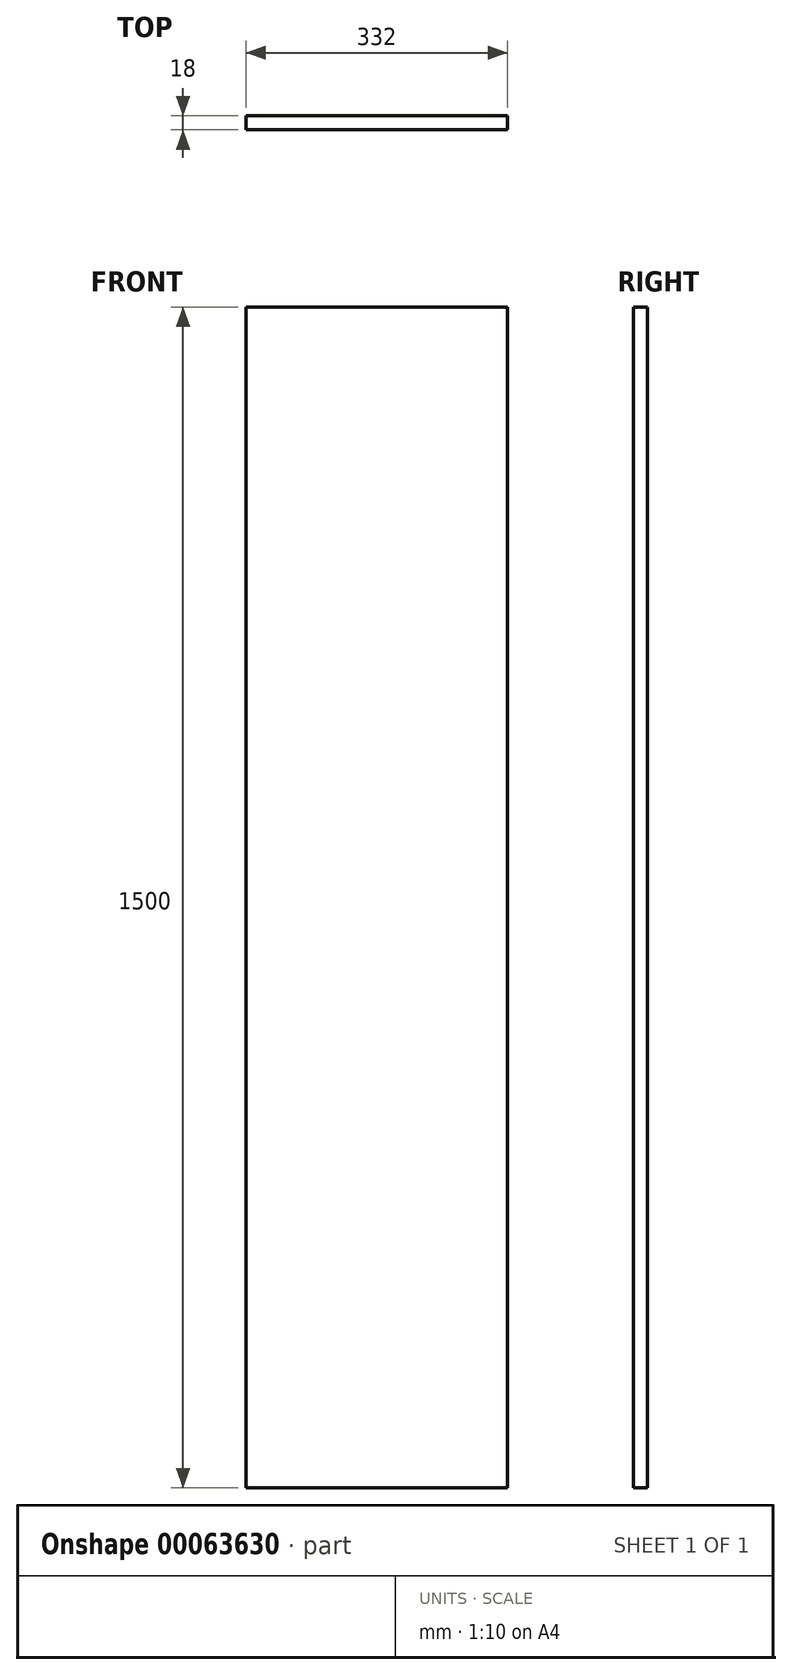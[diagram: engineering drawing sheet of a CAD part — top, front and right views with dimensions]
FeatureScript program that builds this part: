
annotation { "Feature Type Name" : "Feature", "Feature Type Description" : "" }
export const myFeature = defineFeature(function(context is Context, id is Id, definition is map)
    precondition{}
    {
        {
            var Q0;
            Q0=qCreatedBy(makeId("Front.planeOp"),FACE);
            var sketch = newSketch(context, id + "F0", { "sketchPlane" : qUnion([Q0])});
            skLineSegment(sketch, "E0.bottom", {"start": v(0, 0) * mm, "end": v(332, 0) * mm});
            skLineSegment(sketch, "E0.top", {"start": v(0, -1500) * mm, "end": v(332, -1500) * mm});
            skLineSegment(sketch, "E0.left", {"start": v(0, 0) * mm, "end": v(0, -1500) * mm});
            skLineSegment(sketch, "E0.right", {"start": v(332, 0) * mm, "end": v(332, -1500) * mm});
            skSolve(sketch);
        }
        {
            var Q0;
            Q0=qSketchRegion(id+"F0",true);
            extrude(context, id + "F1", {"entities" : qUnion([Q0]), "depth" : 18 * mm});
        }
    });
